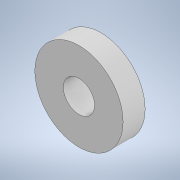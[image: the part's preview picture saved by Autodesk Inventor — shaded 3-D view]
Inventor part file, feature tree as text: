
AUTODESK INVENTOR PART (.ipt)
format: ipt  version: 2020 (Build 240168000, 168)  size: 96,768 bytes
history: native  units: in
note: dims shown in document units (in); Inventor stores cm internally (conversion verified against a paired STEP export)
features: extrude x1, sketch x1
ambient origin geometry x8: Origin, YZ Plane, XZ Plane, XY Plane, X Axis, Y Axis, Z Axis, Center Point
bodies: Solid1 (feature_tree)
feature tree (2):
  extrude  "Extrusion1"  Depth=0.125in
  sketch  "Sketch1"  dims[d0=0.5in d1=0.1772in d2=0.125in d3=0.0in]
